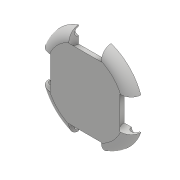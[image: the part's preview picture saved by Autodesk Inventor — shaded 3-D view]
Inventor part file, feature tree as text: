
AUTODESK INVENTOR PART (.ipt)
format: ipt  version: 2017 (Build 210142000, 142)  size: 155,136 bytes
history: native  units: mm
features: sketch x3, extrude x2, revolve x1, fillet x1, pattern_circular x1, projected_geometry x1
ambient origin geometry x8: Origin, YZ Plane, XZ Plane, XY Plane, X Axis, Y Axis, Z Axis, Center Point
bodies: Solid1 (feature_tree)
feature tree (9):
  extrude  "Extrusion1"  Depth=6.0mm TaperAngle=0.0deg
  revolve  "Revolution1"  [1 undecoded]
  extrude  "Extrusion2"  Depth=5.0mm
  fillet  "Fillet1"  Radius=5.0mm
  pattern_circular  "Circular Pattern1"  Angle=90.0deg  [1 undecoded]
  sketch  "Sketch1"  dims[d0=60.0mm d1=6.0mm d2=0.0mm]
  sketch  "Sketch2"  dims[d3=20.0mm d4=25.0mm]
  sketch  "Sketch3"  dims[d5=14.0mm d6=5.0mm d7=5.0mm d8=90.0deg d9=6.0mm d10=0.0mm d11=6.0mm d12=40.0mm d13=360.0deg]
  projected_geometry  "Projected Loop1"
note: 2 required parameter values undecoded (feature->parameter linkage not recoverable at this tier; creation-order binding heuristic only, values carry confidence <= 0.55)